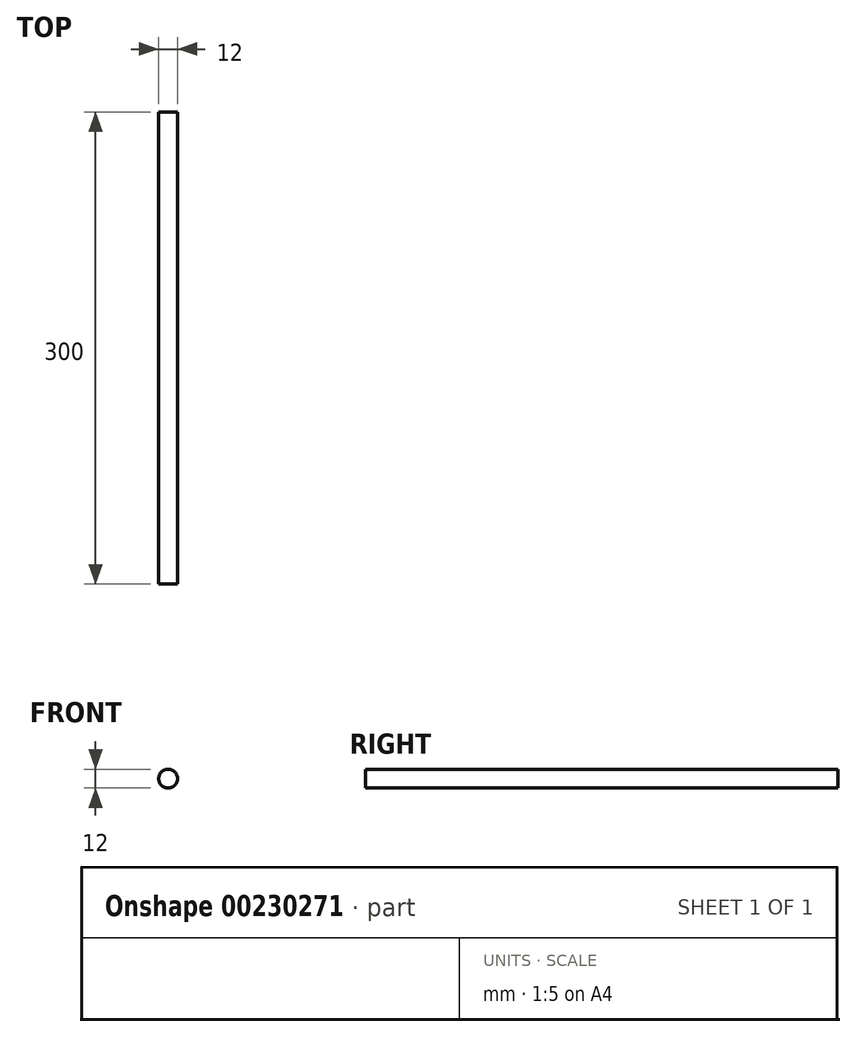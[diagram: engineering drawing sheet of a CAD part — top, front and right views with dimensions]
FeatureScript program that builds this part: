
annotation { "Feature Type Name" : "Feature", "Feature Type Description" : "" }
export const myFeature = defineFeature(function(context is Context, id is Id, definition is map)
    precondition{}
    {
        {
            var Q0;
            Q0=qCreatedBy(makeId("Front.planeOp"),FACE);
            var sketch = newSketch(context, id + "F0", { "sketchPlane" : qUnion([Q0])});
            skCircle(sketch, "E0", {"center": v(0, 0) * mm, "radius": 6 * mm});
            skSolve(sketch);
        }
        {
            var Q0;
            Q0=makeQuery(id+"F0.imprint","IMPRINT",FACE,{"disambiguationData":[TD([[makeQuery(id+"F0.imprint","IMPRINT",EDGE,{"derivedFrom":sQuery(id+"F0.wireOp",EDGE,"E0")}),1.0]])]});
            extrude(context, id + "F1", {"entities" : qUnion([Q0]), "endBound" : BoundingType.SYMMETRIC, "depth" : 300 * mm});
        }
    });
